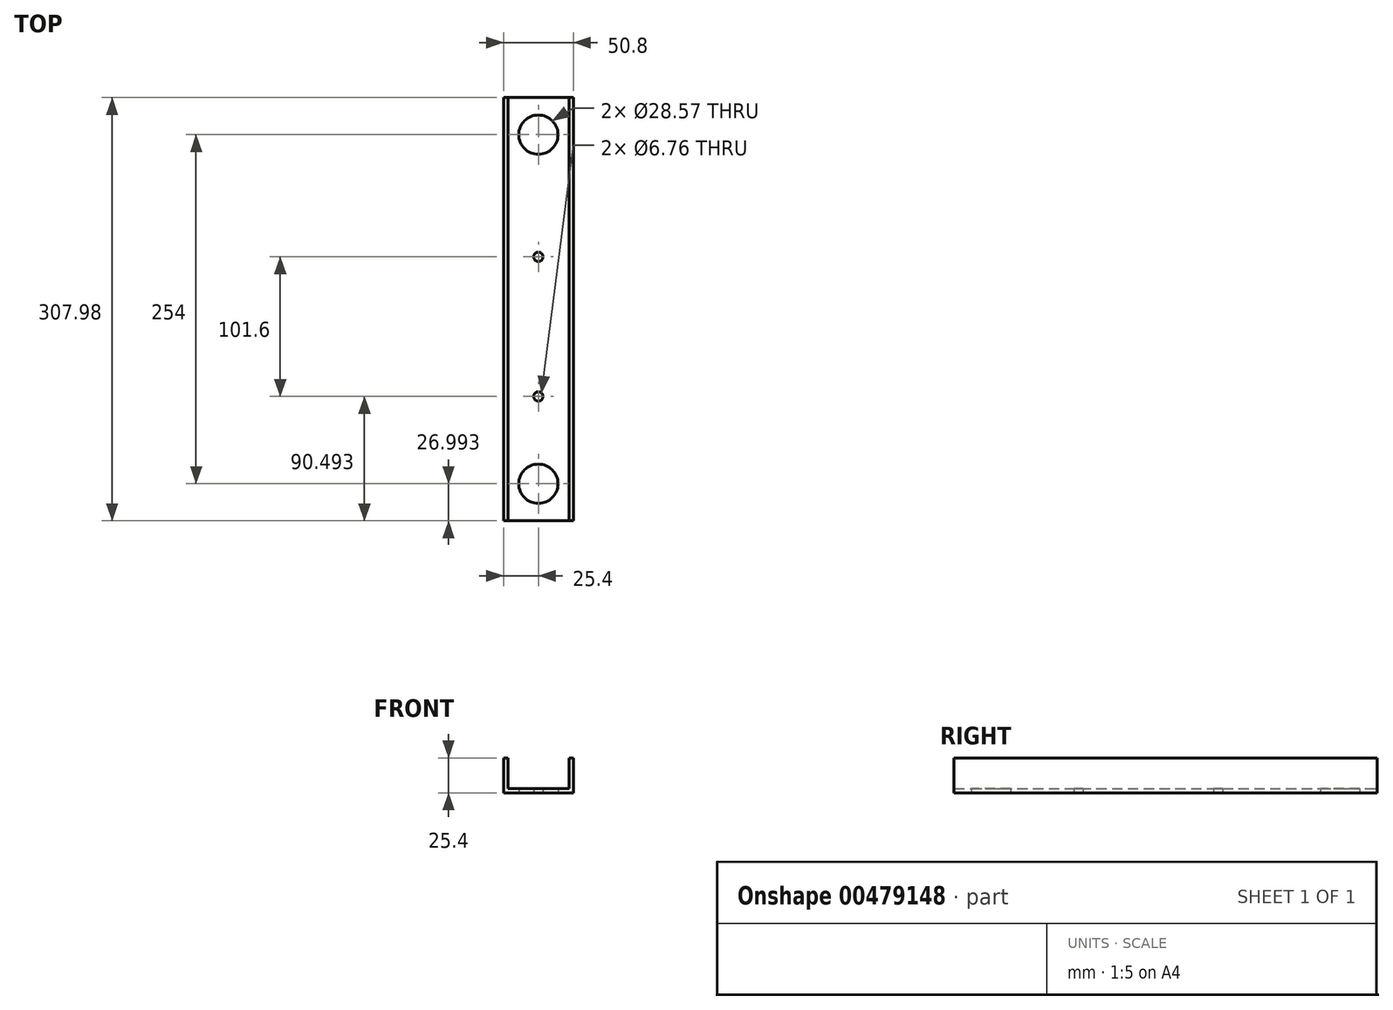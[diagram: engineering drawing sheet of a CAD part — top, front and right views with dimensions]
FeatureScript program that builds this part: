
annotation { "Feature Type Name" : "Feature", "Feature Type Description" : "" }
export const myFeature = defineFeature(function(context is Context, id is Id, definition is map)
    precondition{}
    {
        {
            var Q0;
            Q0=qCreatedBy(makeId("Front.planeOp"),FACE);
            var sketch = newSketch(context, id + "F0", { "sketchPlane" : qUnion([Q0])});
            skLineSegment(sketch, "E0", {"start": v(-44.36, 22.86) * mm, "end": v(-44.36, -2.54) * mm});
            skLineSegment(sketch, "E1", {"start": v(-44.36, -2.54) * mm, "end": v(6.44, -2.54) * mm});
            skLineSegment(sketch, "E2", {"start": v(6.44, -2.54) * mm, "end": v(6.44, 22.86) * mm});
            skLineSegment(sketch, "E3", {"start": v(6.44, 22.86) * mm, "end": v(3.27, 22.86) * mm});
            skLineSegment(sketch, "E4", {"start": v(3.27, 22.86) * mm, "end": v(3.27, 0.63) * mm});
            skLineSegment(sketch, "E5", {"start": v(3.27, 0.63) * mm, "end": v(-41.18, 0.63) * mm});
            skLineSegment(sketch, "E6", {"start": v(-41.18, 0.63) * mm, "end": v(-41.18, 22.86) * mm});
            skLineSegment(sketch, "E7", {"start": v(-41.18, 22.86) * mm, "end": v(-44.36, 22.86) * mm});
            skSolve(sketch);
        }
        {
            var Q0;
            Q0=qSketchRegion(id+"F0",true);
            extrude(context, id + "F1", {"entities" : qUnion([Q0]), "depth" : 307.97 * mm});
        }
        {
            var Q0;
            Q0=makeQuery(id+"F1.opExtrude","SWEPT_FACE",FACE,{"disambiguationData":[OSD([sQuery(id+"F0.wireOp",EDGE,"E1")])]});
            var sketch = newSketch(context, id + "F2", { "sketchPlane" : qUnion([Q0])});
            skPoint(sketch, "E8", {"position": v(-18.96, 26.99) * mm});
            skPoint(sketch, "E9", {"position": v(-18.96, 280.99) * mm});
            skCircle(sketch, "E10", {"center": v(-18.96, 26.99) * mm, "radius": 14.29 * mm});
            skCircle(sketch, "E11", {"center": v(-18.96, 280.99) * mm, "radius": 14.29 * mm});
            skPoint(sketch, "E12", {"position": v(-18.96, 217.49) * mm});
            skPoint(sketch, "E13", {"position": v(-18.96, 115.89) * mm});
            skSolve(sketch);
        }
        {
            var Q0;
            Q0=makeQuery(id+"F2.imprint","IMPRINT",FACE,{"disambiguationData":[TD([[makeQuery(id+"F2.imprint","IMPRINT",EDGE,{"derivedFrom":sQuery(id+"F2.wireOp",EDGE,"E11")}),1.0]])]});
            var Q1;
            Q1=makeQuery(id+"F2.imprint","IMPRINT",FACE,{"disambiguationData":[TD([[makeQuery(id+"F2.imprint","IMPRINT",EDGE,{"derivedFrom":sQuery(id+"F2.wireOp",EDGE,"E10")}),1.0]])]});
            extrude(context, id + "F3", {"entities" : qUnion([Q0, Q1]), "operationType" : NewBodyOperationType.REMOVE, "oppositeDirection" : true, "depth" : 25.4 * mm});
        }
        {
            var Q0;
            Q0=sQuery(id+"F2.wireOp",VERTEX,"E12");
            var Q1;
            Q1=sQuery(id+"F2.wireOp",VERTEX,"E13");
            var Q2;
            Q2=makeQuery(id+"F1.opExtrude","SWEPT_BODY",BODY,{"disambiguationData":[OSD([sQuery(id+"F0.wireOp",EDGE,"E0"),sQuery(id+"F0.wireOp",EDGE,"E1"),sQuery(id+"F0.wireOp",EDGE,"E2"),sQuery(id+"F0.wireOp",EDGE,"E3"),sQuery(id+"F0.wireOp",EDGE,"E4"),sQuery(id+"F0.wireOp",EDGE,"E5"),sQuery(id+"F0.wireOp",EDGE,"E6"),sQuery(id+"F0.wireOp",EDGE,"E7")])]});
            hole(context, id + "F4", {"style" : HoleStyle.SIMPLE, "endStyle" : HoleEndStyle.BLIND, "standardTappedOrClearance" : lookupTablePath({ "standard" : "ANSI", "fit" : "Normal (ASME)", "size" : "1/4", "type" : "Clearance" }), "standardBlindInLast" : lookupTablePath({ "fit" : "Free", "standard" : "ANSI", "size" : "1/4", "type" : "Clearance" }), "holeDiameter" : 6.76 * mm, "holeDepth" : 76.2 * mm, "isTappedThrough" : true, "tappedDepth" : 12.7 * mm, "tapClearance" : 3, "startFromSketch" : true, "locations" : qUnion([Q0, Q1]), "scope" : qUnion([Q2])});
        }
    });
